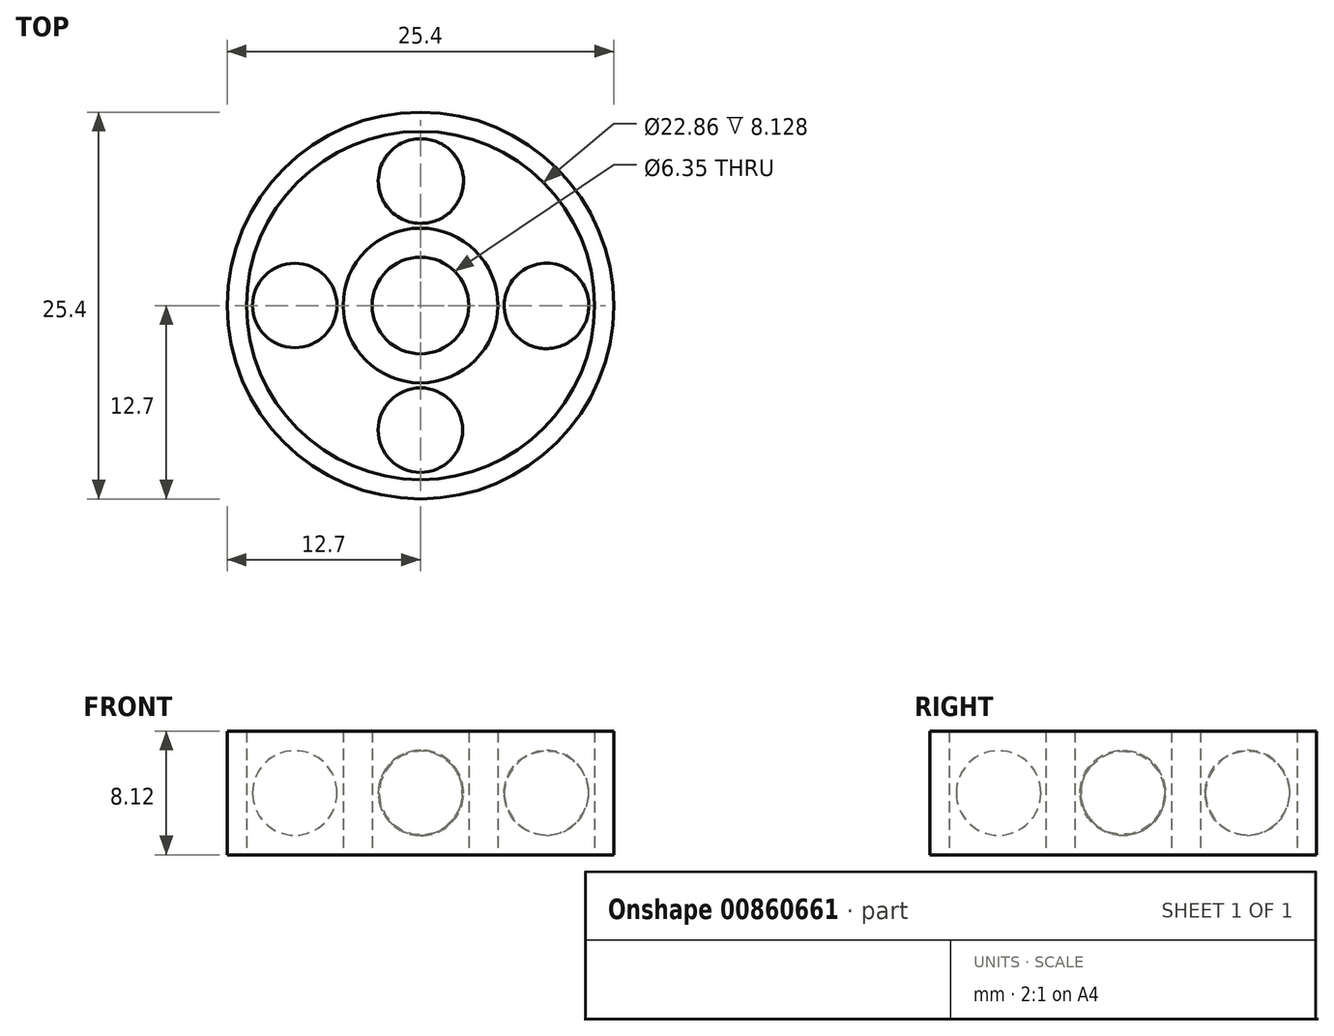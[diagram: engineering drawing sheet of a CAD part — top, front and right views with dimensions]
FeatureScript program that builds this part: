
annotation { "Feature Type Name" : "Feature", "Feature Type Description" : "" }
export const myFeature = defineFeature(function(context is Context, id is Id, definition is map)
    precondition{}
    {
        {
            var Q0;
            Q0=qCreatedBy(makeId("Top.planeOp"),FACE);
            var sketch = newSketch(context, id + "F0", { "sketchPlane" : qUnion([Q0])});
            skCircle(sketch, "E0", {"center": v(0, 0) * mm, "radius": 12.7 * mm});
            skCircle(sketch, "E1", {"center": v(0, 0) * mm, "radius": 11.43 * mm});
            skCircle(sketch, "E2", {"center": v(0, 0) * mm, "radius": 3.18 * mm});
            skCircle(sketch, "E3", {"center": v(0, 0) * mm, "radius": 5.08 * mm});
            skCircle(sketch, "E4", {"center": v(-8.26, 0) * mm, "radius": 2.77 * mm});
            skCircle(sketch, "E5", {"center": v(8.28, 0) * mm, "radius": 2.77 * mm});
            skCircle(sketch, "E6", {"center": v(0.06, 8.17) * mm, "radius": 2.77 * mm});
            skCircle(sketch, "E7", {"center": v(0, -8.19) * mm, "radius": 2.77 * mm});
            skLineSegment(sketch, "E8", {"start": v(-11.43, 0) * mm, "end": v(-5.08, 0) * mm});
            skLineSegment(sketch, "E9", {"start": v(0, 5.4) * mm, "end": v(0.06, 10.94) * mm});
            skLineSegment(sketch, "E10", {"start": v(5.5, 0) * mm, "end": v(11.05, -0.06) * mm});
            skLineSegment(sketch, "E11", {"start": v(0, -5.41) * mm, "end": v(0, -10.96) * mm});
            skCircle(sketch, "E12", {"center": v(-5.75, 5.84) * mm, "radius": 2.77 * mm});
            skSolve(sketch);
        }
        {
            var Q0;
            Q0=makeQuery(id+"F0.imprint","IMPRINT",FACE,{"disambiguationData":[TD([[makeQuery(id+"F0.imprint","IMPRINT",EDGE,{"derivedFrom":sQuery(id+"F0.wireOp",EDGE,"E0")}),1.0]])]});
            var Q1;
            Q1=makeQuery(id+"F0.imprint","IMPRINT",FACE,{"disambiguationData":[TD([[makeQuery(id+"F0.imprint","IMPRINT",EDGE,{"derivedFrom":sQuery(id+"F0.wireOp",EDGE,"E2")}),-1.0]])]});
            extrude(context, id + "F1", {"entities" : qUnion([Q0, Q1]), "endBound" : BoundingType.SYMMETRIC, "depth" : 8.13 * mm, "offsetDistance" : 25.4 * mm});
        }
        {
            var Q0;
            {var subQ0=sQuery(id+"F0.wireOp",EDGE,"E9");Q0=makeQuery(id+"F0.imprint","IMPRINT",FACE,{"disambiguationData":[TD([[makeQuery(id+"F0.imprint","IMPRINT",EDGE,{"derivedFrom":subQ0}),1.0]])]});}
            var Q1;
            Q1=sQuery(id+"F0.wireOp",EDGE,"E9");
            revolve(context, id + "F2", {"surfaceOperationType" : NewSurfaceOperationType.NEW, "entities" : qUnion([Q0]), "axis" : qUnion([Q1]), "revolveType" : RevolveType.FULL});
        }
        {
            var Q0;
            {var subQ0=sQuery(id+"F0.wireOp",EDGE,"E11");Q0=makeQuery(id+"F0.imprint","IMPRINT",FACE,{"disambiguationData":[TD([[makeQuery(id+"F0.imprint","IMPRINT",EDGE,{"derivedFrom":subQ0}),-1.0]])]});}
            var Q1;
            Q1=sQuery(id+"F0.wireOp",EDGE,"E11");
            revolve(context, id + "F3", {"surfaceOperationType" : NewSurfaceOperationType.NEW, "entities" : qUnion([Q0]), "axis" : qUnion([Q1]), "revolveType" : RevolveType.FULL});
        }
        {
            var Q0;
            {var subQ0=sQuery(id+"F0.wireOp",EDGE,"E8");var subQ1=sQuery(id+"F0.wireOp",EDGE,"E4");var subQ2=makeQuery(id+"F0.imprint","INTERSECT",VERTEX,{"disambiguationData":[OD(0.0)],"derivedFrom":[subQ1,subQ0]});Q0=makeQuery(id+"F0.imprint","IMPRINT",FACE,{"disambiguationData":[TD([[makeQuery(id+"F0.imprint","IMPRINT",EDGE,{"disambiguationData":[TD([[subQ2,1.0]])],"derivedFrom":subQ1}),1.0]])]});}
            var Q1;
            Q1=sQuery(id+"F0.wireOp",EDGE,"E8");
            revolve(context, id + "F4", {"surfaceOperationType" : NewSurfaceOperationType.NEW, "entities" : qUnion([Q0]), "axis" : qUnion([Q1]), "revolveType" : RevolveType.FULL});
        }
        {
            var Q0;
            {var subQ0=sQuery(id+"F0.wireOp",EDGE,"E10");Q0=makeQuery(id+"F0.imprint","IMPRINT",FACE,{"disambiguationData":[TD([[makeQuery(id+"F0.imprint","IMPRINT",EDGE,{"derivedFrom":subQ0}),1.0]])]});}
            var Q1;
            Q1=sQuery(id+"F0.wireOp",EDGE,"E10");
            revolve(context, id + "F5", {"surfaceOperationType" : NewSurfaceOperationType.NEW, "entities" : qUnion([Q0]), "axis" : qUnion([Q1]), "revolveType" : RevolveType.FULL});
        }
        {
            var Q0;
            {var subQ0=sQuery(id+"F0.wireOp",EDGE,"E11");Q0=makeQuery(id+"F0.imprint","IMPRINT",FACE,{"disambiguationData":[TD([[makeQuery(id+"F0.imprint","IMPRINT",EDGE,{"derivedFrom":subQ0}),1.0]])]});}
            var Q1;
            Q1=sQuery(id+"F0.wireOp",EDGE,"E11");
            revolve(context, id + "F6", {"surfaceOperationType" : NewSurfaceOperationType.NEW, "entities" : qUnion([Q0]), "axis" : qUnion([Q1]), "revolveType" : RevolveType.FULL});
        }
    });
